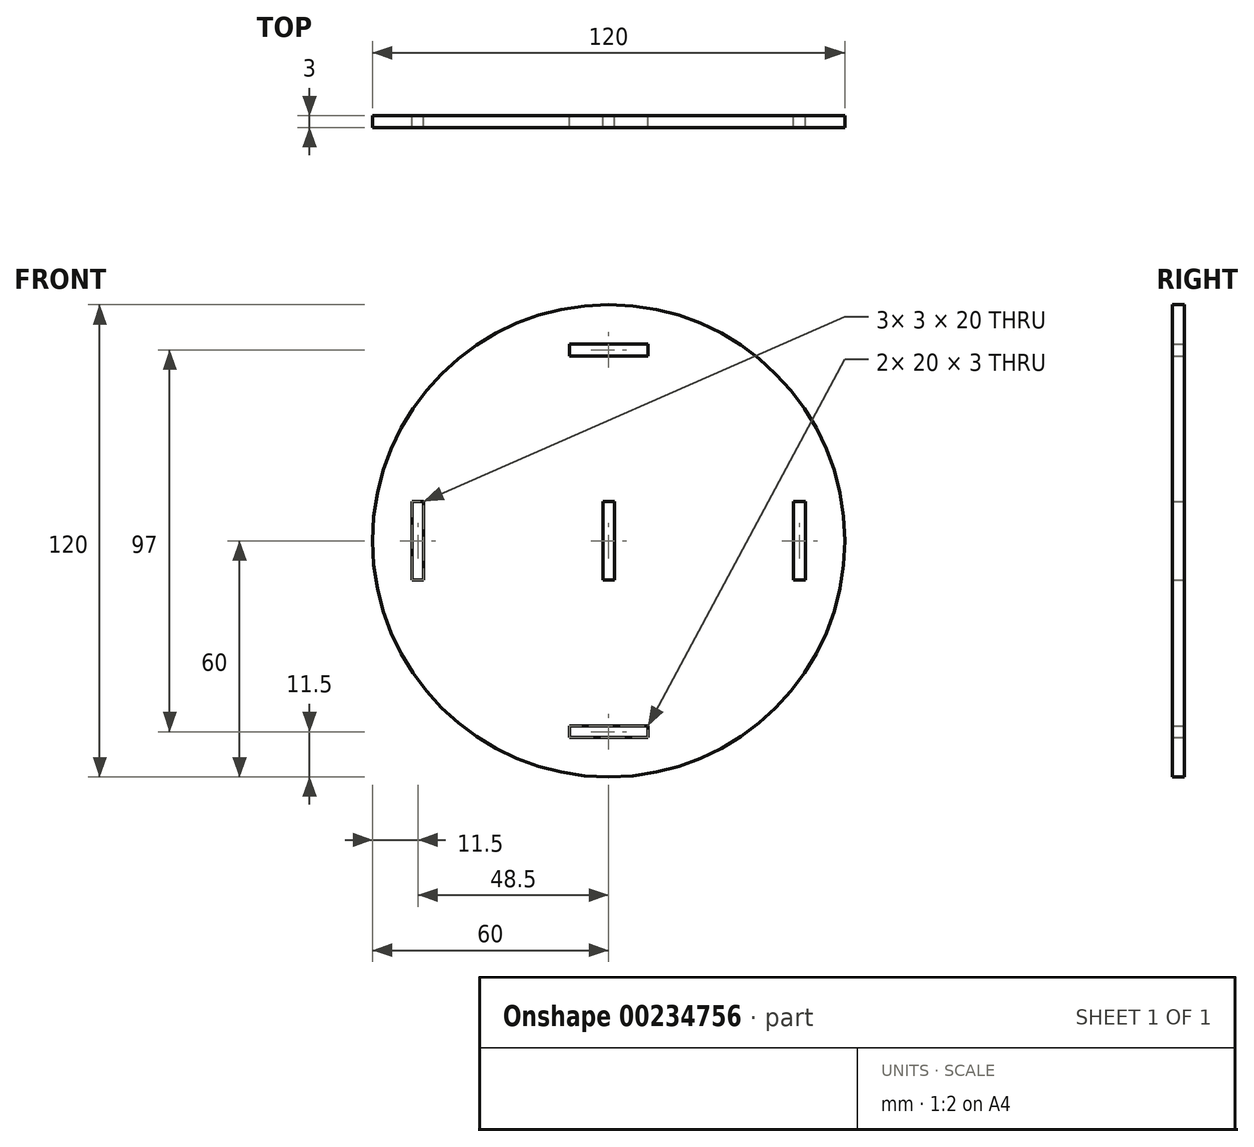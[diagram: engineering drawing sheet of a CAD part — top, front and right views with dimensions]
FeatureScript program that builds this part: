
annotation { "Feature Type Name" : "Feature", "Feature Type Description" : "" }
export const myFeature = defineFeature(function(context is Context, id is Id, definition is map)
    precondition{}
    {
        {
            var Q0;
            Q0=qCreatedBy(makeId("Front.planeOp"),FACE);
            var sketch = newSketch(context, id + "F0", { "sketchPlane" : qUnion([Q0])});
            skCircle(sketch, "E0", {"center": v(0, 0) * mm, "radius": 60 * mm});
            skLineSegment(sketch, "E1.bottom", {"start": v(1.5, 10) * mm, "end": v(-1.5, 10) * mm});
            skLineSegment(sketch, "E1.top", {"start": v(1.5, -10) * mm, "end": v(-1.5, -10) * mm});
            skLineSegment(sketch, "E1.left", {"start": v(1.5, 10) * mm, "end": v(1.5, -10) * mm});
            skLineSegment(sketch, "E1.right", {"start": v(-1.5, 10) * mm, "end": v(-1.5, -10) * mm});
            skLineSegment(sketch, "E2.bottom", {"start": v(-10, -47) * mm, "end": v(10, -47) * mm});
            skLineSegment(sketch, "E2.top", {"start": v(-10, -50) * mm, "end": v(10, -50) * mm});
            skLineSegment(sketch, "E2.left", {"start": v(-10, -47) * mm, "end": v(-10, -50) * mm});
            skLineSegment(sketch, "E2.right", {"start": v(10, -47) * mm, "end": v(10, -50) * mm});
            skPoint(sketch, "E2.middle", {"position": v(0, -48.5) * mm});
            skLineSegment(sketch, "E3.bottom", {"start": v(-47, 10) * mm, "end": v(-50, 10) * mm});
            skLineSegment(sketch, "E3.top", {"start": v(-47, -10) * mm, "end": v(-50, -10) * mm});
            skLineSegment(sketch, "E3.left", {"start": v(-47, 10) * mm, "end": v(-47, -10) * mm});
            skLineSegment(sketch, "E3.right", {"start": v(-50, 10) * mm, "end": v(-50, -10) * mm});
            skPoint(sketch, "E3.middle", {"position": v(-48.5, 0) * mm});
            skLineSegment(sketch, "E4.bottom", {"start": v(-10, 50) * mm, "end": v(10, 50) * mm});
            skLineSegment(sketch, "E4.top", {"start": v(-10, 47) * mm, "end": v(10, 47) * mm});
            skLineSegment(sketch, "E4.left", {"start": v(-10, 50) * mm, "end": v(-10, 47) * mm});
            skLineSegment(sketch, "E4.right", {"start": v(10, 50) * mm, "end": v(10, 47) * mm});
            skPoint(sketch, "E4.middle", {"position": v(0, 48.5) * mm});
            skLineSegment(sketch, "E5.bottom", {"start": v(51.66, 30.5) * mm, "end": v(51.02, 30.5) * mm});
            skLineSegment(sketch, "E6.right", {"start": v(59.62, 8.7) * mm, "end": v(59.62, -8.7) * mm});
            skLineSegment(sketch, "E7.bottom", {"start": v(50, 10) * mm, "end": v(47, 10) * mm});
            skLineSegment(sketch, "E7.top", {"start": v(50, -10) * mm, "end": v(47, -10) * mm});
            skLineSegment(sketch, "E7.left", {"start": v(50, 10) * mm, "end": v(50, -10) * mm});
            skLineSegment(sketch, "E7.right", {"start": v(47, 10) * mm, "end": v(47, -10) * mm});
            skPoint(sketch, "E7.middle", {"position": v(48.5, 0) * mm});
            skSolve(sketch);
        }
        {
            var Q0;
            Q0 = qSketchRegion(id + "F0", true);
            extrude(context, id + "F1", {"entities" : qUnion([Q0]), "depth" : 3 * mm});
        }
        {
            var Q0;
            Q0 = qSketchRegion(id + "F0", true);
            extrude(context, id + "F2", {"entities" : qUnion([Q0]), "operationType" : NewBodyOperationType.ADD, "depth" : 3 * mm});
        }
    });
